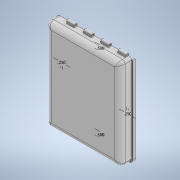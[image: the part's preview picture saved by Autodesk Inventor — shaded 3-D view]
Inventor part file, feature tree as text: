
AUTODESK INVENTOR PART (.ipt)
format: ipt  version: 2022 (Build 260153000, 153)  size: 310,272 bytes
history: native  units: in
note: dims shown in document units (in); Inventor stores cm internally (conversion verified against a paired STEP export)
features: sketch x12, extrude x11, plane x5, fillet x4, projected_geometry x4
ambient origin geometry x8: Origin, YZ Plane, XZ Plane, XY Plane, X Axis, Y Axis, Z Axis, Center Point
bodies: Solid1 (feature_tree)
feature tree (36):
  extrude  "Extrusion1"  Depth=8.6in
  extrude  "Extrusion2"  Depth=1.11in TaperAngle=0.0deg
  fillet  "Fillet1"  Radius=0.125in
  fillet  "Fillet3"  Radius=0.125in
  fillet  "Fillet4"  Radius=0.5in
  sketch  "Sketch4"  dims[d13=0.25in d14=0.125in]
  sketch  "Sketch5"  dims[d17=0.5in d18=0.5in]
  plane  "Work Plane1"
  plane  "Work Plane2"
  plane  "Work Plane5"
  extrude  "Extrusion5"  Depth=0.25in
  sketch  "Sketch14"  dims[d21=0.25in d22=6.5in d23=1.625in]
  sketch  "Sketch15"  dims[d24=1.625in d25=1.625in d26=0.25in]
  sketch  "Sketch16"  dims[d27=0.25in d28=6.5in d29=0.0in]
  sketch  "Sketch17"  dims[d58=0.25in d59=0.25in]
  extrude  "Extrusion12"  Depth=0.5in
  extrude  "Extrusion13"  Depth=0.25in
  extrude  "Extrusion14"  Depth=0.25in
  extrude  "Extrusion15"  Depth=0.25in
  extrude  "Extrusion16"  Depth=0.25in TaperAngle=0.0deg
  extrude  "Extrusion17"  Depth=0.25in
  extrude  "Extrusion18"  Depth=0.25in
  extrude  "Extrusion19"  Depth=0.25in
  fillet  "Fillet6"  Radius=0.25in
  sketch  "Sketch1"  dims[d0=7.006in d1=8.6in]
  sketch  "Sketch2"  dims[d2=0.5in d3=1.11in d4=0.0in d5=0.125in d6=0.0in d10=0.125in d12=0.5in]
  projected_geometry  "Projected Loop1"
  plane  "Work Plane3"
  plane  "Work Plane4"
  sketch  "Sketch6"  dims[d19=0.25in d20=0.25in]
  sketch  "Sketch18"  dims[d60=0.125in d61=0.25in]
  sketch  "Sketch19"  dims[d62=0.25in d63=0.125in d64=0.25in]
  projected_geometry  "Projected Loop7"
  projected_geometry  "Projected Loop8"
  projected_geometry  "Projected Loop9"
  sketch  "Sketch20"  dims[d65=0.25in d66=0.125in d67=0.25in d68=0.25in d69=0.125in d70=0.7625in d71=0.0in d72=0.7625in d73=0.0in d74=0.7625in d75=0.0in d76=0.7625in d77=0.0in d78=0.2in d79=0.125in d80=5.5875in d81=0.0in d82=0.25in d83=0.0in d84=0.25in d85=0.0in d90=0.05in d91=0.0in d92=0.1in d86=0.0in d87=0.0in]
